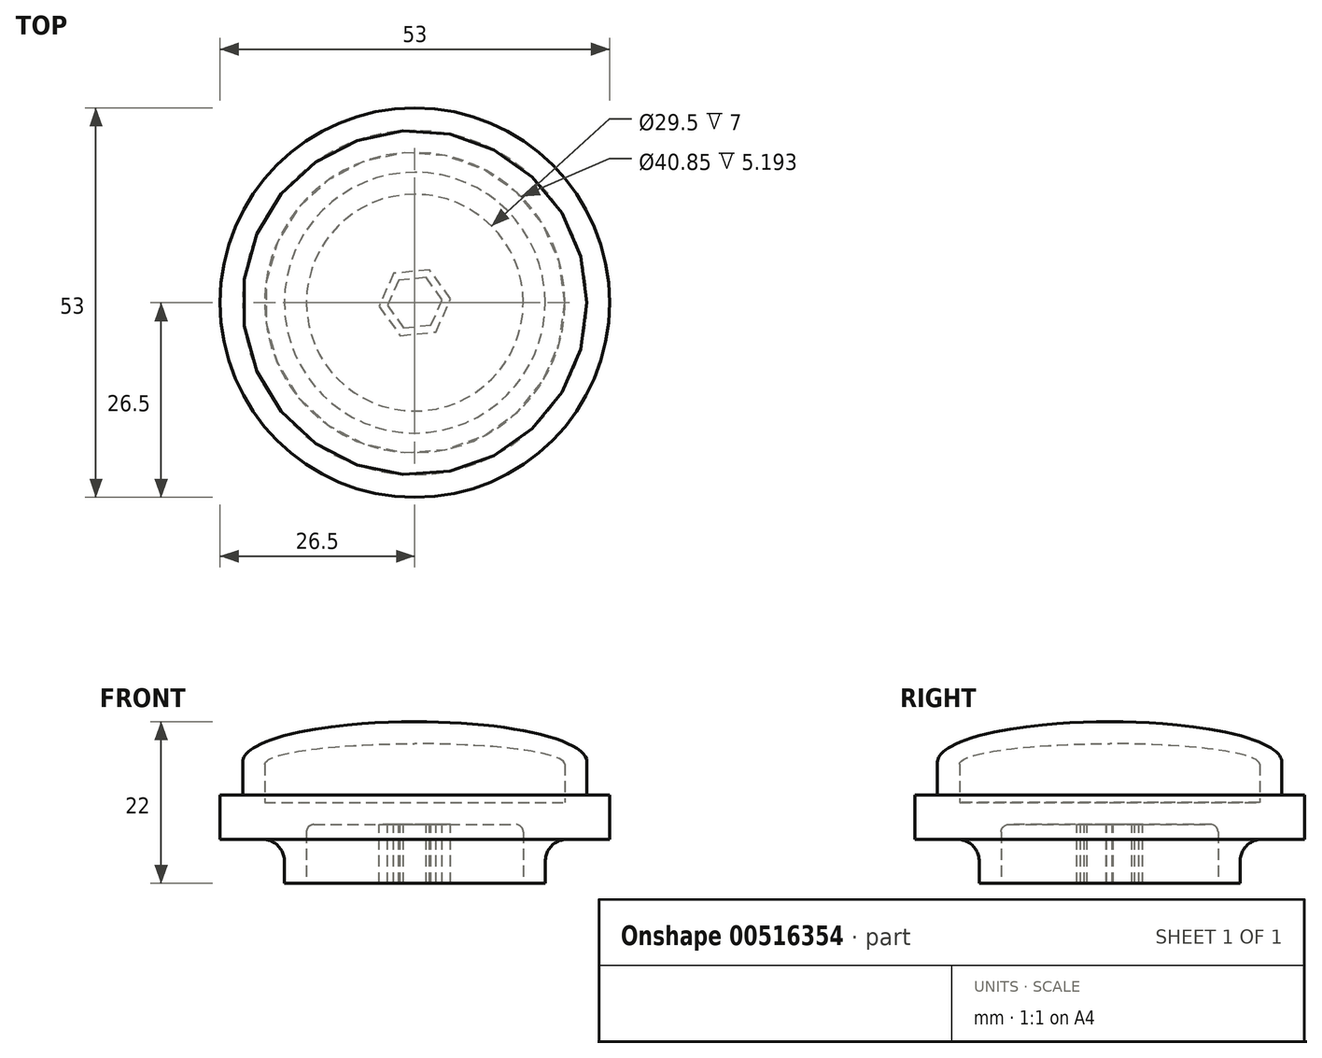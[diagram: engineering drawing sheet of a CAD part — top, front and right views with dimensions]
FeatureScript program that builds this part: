
annotation { "Feature Type Name" : "Feature", "Feature Type Description" : "" }
export const myFeature = defineFeature(function(context is Context, id is Id, definition is map)
    precondition{}
    {
        {
            var Q0;
            Q0=qCreatedBy(makeId("Front.planeOp"),FACE);
            var sketch = newSketch(context, id + "F0", { "sketchPlane" : qUnion([Q0])});
            skLineSegment(sketch, "E0", {"start": v(0, 0) * mm, "end": v(0, 6) * mm, "construction": true});
            skLineSegment(sketch, "E1", {"start": v(20.75, 0) * mm, "end": v(26.5, 0) * mm});
            skLineSegment(sketch, "E2", {"start": v(26.5, 0) * mm, "end": v(26.5, 6) * mm});
            skLineSegment(sketch, "E3", {"start": v(26.5, 6) * mm, "end": v(23.43, 6) * mm});
            skLineSegment(sketch, "E4", {"start": v(23.43, 6) * mm, "end": v(23.43, 10.5) * mm});
            skEllipticalArc(sketch, "E5", {});
            skPoint(sketch, "E6", {"position": v(23.43, 10.5) * mm});
            skLineSegment(sketch, "E7", {"start": v(0, 16) * mm, "end": v(0, 13) * mm});
            skLineSegment(sketch, "E8", {"start": v(14.75, -6) * mm, "end": v(14.75, 1) * mm});
            skLineSegment(sketch, "E9", {"start": v(14.75, 6) * mm, "end": v(0, 6) * mm, "construction": true});
            skPoint(sketch, "E9.endSnap0", {"position": v(24.96, 6) * mm});
            skLineSegment(sketch, "E10", {"start": v(0, 2) * mm, "end": v(13.75, 2) * mm});
            skLineSegment(sketch, "E11", {"start": v(14.75, -6) * mm, "end": v(17.75, -6) * mm});
            skLineSegment(sketch, "E12", {"start": v(17.75, -6) * mm, "end": v(17.75, -3) * mm});
            skPoint(sketch, "E13.visualSharp", {"position": v(17.75, 0) * mm});
            skArc(sketch, "E13.filletArc", {"start": v(20.75, 0) * mm, "mid": v(18.63, -0.88) * mm, "end": v(17.75, -3) * mm});
            skLineSegment(sketch, "E14", {"start": v(0, 2) * mm, "end": v(0, 6) * mm});
            skPoint(sketch, "E15.visualSharp", {"position": v(14.75, 2) * mm});
            skArc(sketch, "E15.filletArc", {"start": v(14.75, 1) * mm, "mid": v(14.46, 1.7) * mm, "end": v(13.75, 2) * mm});
            skLineSegment(sketch, "E16", {"start": v(20.43, 10.2) * mm, "end": v(20.43, 5) * mm});
            skLineSegment(sketch, "E17", {"start": v(20.43, 5) * mm, "end": v(0, 5) * mm});
            skEllipticalArc(sketch, "E18", {});
            skPoint(sketch, "E19", {"position": v(0, 13) * mm});
            skPoint(sketch, "E20.orphan", {"position": v(20.43, 10.5) * mm});
            skLineSegment(sketch, "E21", {"start": v(20.42, 10.2) * mm, "end": v(20.42, 13.2) * mm, "construction": true});
            skLineSegment(sketch, "E22.trimOffspring", {"start": v(0, 13) * mm, "end": v(0, 16) * mm, "construction": true});
            skLineSegment(sketch, "E23.trimOffspring", {"start": v(0, 10.2) * mm, "end": v(0, 10) * mm});
            const initialGuessF0  = {"E5": [0, 0.0105, 0, 1, 0.0055, 0.023425, 4.71238898038469, 6.283185307179586], "E18": [0, 0.010192951402634898, 1, 0, 0.020425, 0.002807048597365102, 0, 1.5707963267948966]};
            skSetInitialGuess(sketch, initialGuessF0);
            skSolve(sketch);
        }
        {
            var Q0;
            Q0 = qSketchRegion(id + "F0", true);
            var Q1;
            Q1=sQuery(id+"F0.wireOp",EDGE,"E0");
            revolve(context, id + "F1", {"entities" : qUnion([Q0]), "axis" : qUnion([Q1]), "revolveType" : RevolveType.FULL});
        }
        {
            var Q0;
            Q0=makeQuery(id+"F1.opRevolve","SWEPT_FACE",FACE,{"disambiguationData":[OSD([sQuery(id+"F0.wireOp",EDGE,"E10")])]});
            var sketch = newSketch(context, id + "F2", { "sketchPlane" : qUnion([Q0])});
            skCircle(sketch, "E24.cCircle", {"center": v(0, 0) * mm, "radius": 3.25 * mm, "construction": true});
            skLineSegment(sketch, "E24.0", {"start": v(2.19, 3.05) * mm, "end": v(3.73, -0.37) * mm});
            skLineSegment(sketch, "E24.1", {"start": v(3.73, -0.37) * mm, "end": v(1.54, -3.42) * mm});
            skLineSegment(sketch, "E24.2", {"start": v(1.54, -3.42) * mm, "end": v(-2.19, -3.05) * mm});
            skLineSegment(sketch, "E24.3", {"start": v(-2.19, -3.05) * mm, "end": v(-3.73, 0.37) * mm});
            skLineSegment(sketch, "E24.4", {"start": v(-3.73, 0.37) * mm, "end": v(-1.54, 3.42) * mm});
            skLineSegment(sketch, "E24.5", {"start": v(-1.54, 3.42) * mm, "end": v(2.19, 3.05) * mm});
            skPoint(sketch, "E24.0.midPoint", {"position": v(2.96, 1.34) * mm});
            skLineSegment(sketch, "E25.0", {"start": v(-2.02, 4.47) * mm, "end": v(2.86, 3.99) * mm});
            skLineSegment(sketch, "E25.1", {"start": v(4.88, -0.49) * mm, "end": v(2.02, -4.47) * mm});
            skLineSegment(sketch, "E25.2", {"start": v(2.02, -4.47) * mm, "end": v(-2.86, -3.99) * mm});
            skLineSegment(sketch, "E25.3", {"start": v(2.86, 3.99) * mm, "end": v(4.88, -0.49) * mm});
            skLineSegment(sketch, "E25.4", {"start": v(-2.86, -3.99) * mm, "end": v(-4.88, 0.49) * mm});
            skLineSegment(sketch, "E25.5", {"start": v(-4.88, 0.49) * mm, "end": v(-2.02, 4.47) * mm});
            skCircle(sketch, "E26.0", {"center": v(0, 0) * mm, "radius": 18.75 * mm});
            skSolve(sketch);
        }
        {
            var Q0;
            Q0=makeQuery(id+"F2.imprint","IMPRINT",FACE,{"disambiguationData":[TD([[makeQuery(id+"F2.imprint","IMPRINT",EDGE,{"derivedFrom":sQuery(id+"F2.wireOp",EDGE,"E24.0")}),1.0]])]});
            var Q1;
            Q1=makeQuery(id+"F1.opRevolve","SWEPT_FACE",FACE,{"disambiguationData":[OSD([sQuery(id+"F0.wireOp",EDGE,"E11")])]});
            extrude(context, id + "F3", {"entities" : qUnion([Q0]), "operationType" : NewBodyOperationType.ADD, "endBound" : BoundingType.UP_TO_SURFACE, "depth" : 25 * mm, "endBoundEntityFace" : qUnion([Q1]), "offsetDistance" : 25 * mm});
        }
    });
